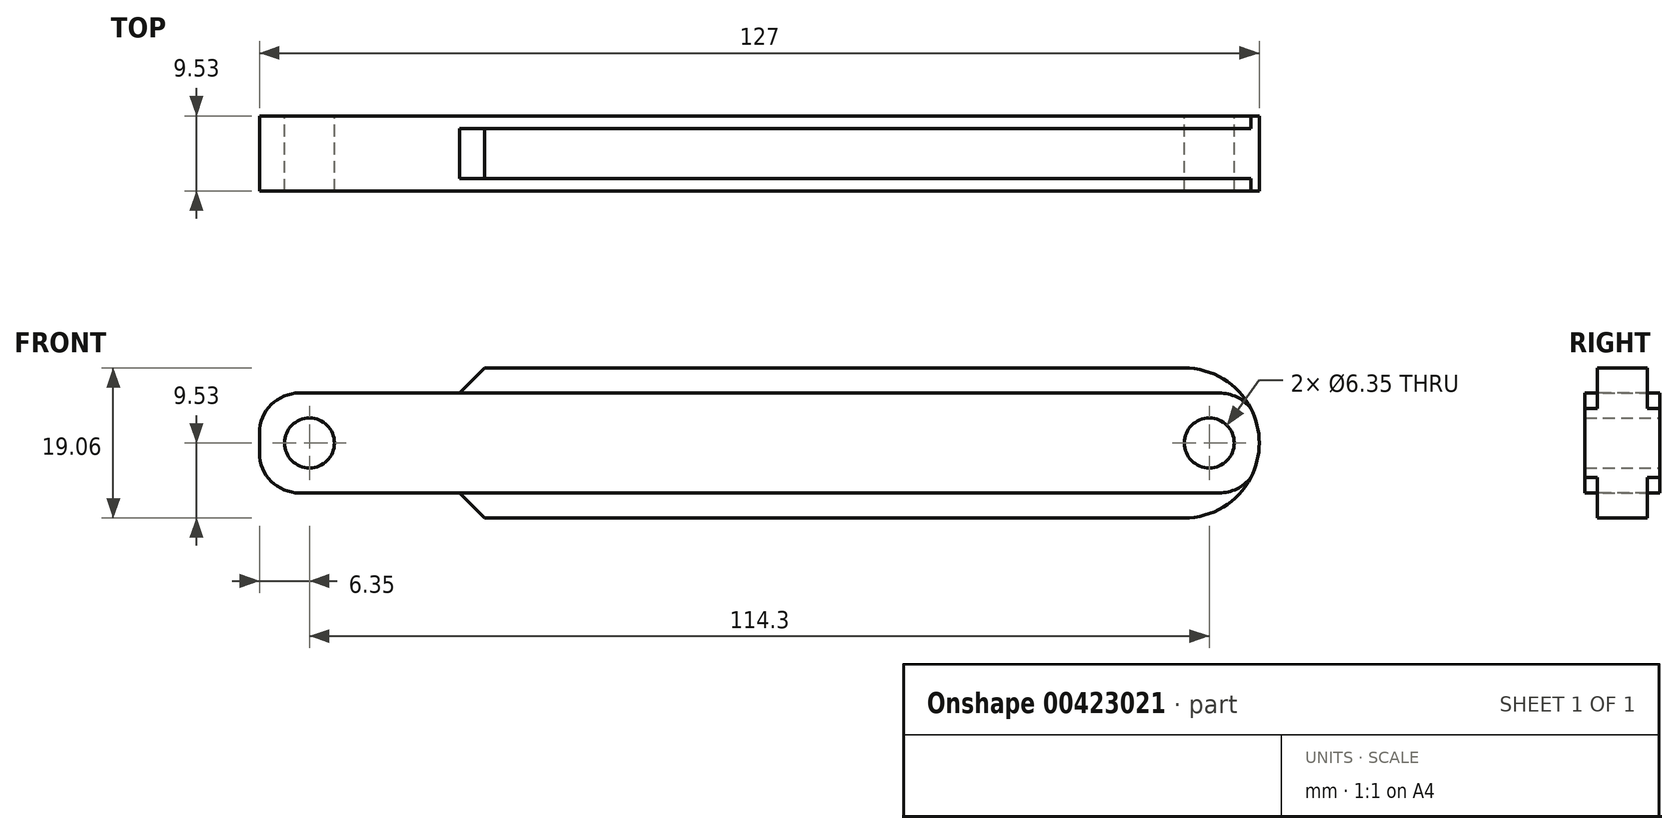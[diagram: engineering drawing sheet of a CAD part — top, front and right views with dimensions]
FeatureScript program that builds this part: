
annotation { "Feature Type Name" : "Feature", "Feature Type Description" : "" }
export const myFeature = defineFeature(function(context is Context, id is Id, definition is map)
    precondition{}
    {
        {
            var Q0;
            Q0=qCreatedBy(makeId("Front.planeOp"),FACE);
            var sketch = newSketch(context, id + "F0", { "sketchPlane" : qUnion([Q0])});
            skLineSegment(sketch, "E0.bottom", {"start": v(63.5, 6.35) * mm, "end": v(-63.5, 6.35) * mm});
            skLineSegment(sketch, "E0.top", {"start": v(63.5, -6.35) * mm, "end": v(-63.5, -6.35) * mm});
            skLineSegment(sketch, "E0.left", {"start": v(63.5, 6.35) * mm, "end": v(63.5, -6.35) * mm});
            skLineSegment(sketch, "E0.right", {"start": v(-63.5, 6.35) * mm, "end": v(-63.5, -6.35) * mm});
            skPoint(sketch, "E0.middle", {"position": v(0, 0) * mm});
            skCircle(sketch, "E1", {"center": v(-57.15, 0) * mm, "radius": 3.18 * mm});
            skCircle(sketch, "E2", {"center": v(57.15, 0) * mm, "radius": 3.18 * mm});
            skSolve(sketch);
        }
        {
            var Q0;
            Q0=qSketchRegion(id+"F0",true);
            extrude(context, id + "F1", {"entities" : qUnion([Q0]), "depth" : 9.52 * mm});
        }
        {
            var Q0;
            Q0=makeQuery(id+"F1.opExtrude","SWEPT_EDGE",EDGE,{"disambiguationData":[OSD([sQuery(id+"F0.wireOp",EDGE,"E0.bottom"),sQuery(id+"F0.wireOp",EDGE,"E0.right")])]});
            var Q1;
            Q1=makeQuery(id+"F1.opExtrude","SWEPT_EDGE",EDGE,{"disambiguationData":[OSD([sQuery(id+"F0.wireOp",EDGE,"E0.top"),sQuery(id+"F0.wireOp",EDGE,"E0.right")])]});
            var Q2;
            Q2=makeQuery(id+"F1.opExtrude","SWEPT_EDGE",EDGE,{"disambiguationData":[OSD([sQuery(id+"F0.wireOp",EDGE,"E0.bottom"),sQuery(id+"F0.wireOp",EDGE,"E0.left")])]});
            var Q3;
            Q3=makeQuery(id+"F1.opExtrude","SWEPT_EDGE",EDGE,{"disambiguationData":[OSD([sQuery(id+"F0.wireOp",EDGE,"E0.top"),sQuery(id+"F0.wireOp",EDGE,"E0.left")])]});
            fillet(context, id + "F2", {"entities" : qUnion([Q0, Q1, Q2, Q3]), "radius" : 5.08 * mm, "tangentPropagation" : true, "allowEdgeOverflow" : false});
        }
        {
            var Q0;
            Q0=qCreatedBy(makeId("Top.planeOp"),FACE);
            var sketch = newSketch(context, id + "F3", { "sketchPlane" : qUnion([Q0])});
            skLineSegment(sketch, "E3", {"start": v(-128.39, -4.76) * mm, "end": v(129.82, -4.76) * mm});
            skSolve(sketch);
        }
        {
            var Q0;
            Q0=qBodyType(qCreatedBy(id+"F3",EDGE),BodyType.WIRE);
            var Q1;
            Q1=makeQuery(id+"F1.opExtrude","SWEPT_FACE",FACE,{"disambiguationData":[OSD([sQuery(id+"F0.wireOp",EDGE,"E0.bottom")])]});
            cPlane(context, id + "F4", {"entities" : qUnion([Q0, Q1]), "cplaneType" : CPlaneType.LINE_ANGLE, "offset" : 25.4 * mm, "angle" : 90 * degree, "width" : 152.4 * mm, "height" : 152.4 * mm});
        }
        {
            var Q0;
            Q0=qCreatedBy(id+"F4.planeOp",FACE);
            var sketch = newSketch(context, id + "F5", { "sketchPlane" : qUnion([Q0])});
            skLineSegment(sketch, "E4.bottom", {"start": v(-63.5, -9.52) * mm, "end": v(38.1, -9.52) * mm});
            skLineSegment(sketch, "E4.top", {"start": v(-63.5, 9.53) * mm, "end": v(38.1, 9.53) * mm});
            skLineSegment(sketch, "E4.left", {"start": v(-63.5, -9.52) * mm, "end": v(-63.5, 9.53) * mm});
            skLineSegment(sketch, "E4.right", {"start": v(38.1, -9.52) * mm, "end": v(38.1, 9.53) * mm});
            skArc(sketch, "E5", {"start": v(-57.06, -4.04) * mm, "mid": v(-52.92, 0.1) * mm, "end": v(-57.1, 4.18) * mm});
            skArc(sketch, "E6", {"start": v(-57.1, 4.18) * mm, "mid": v(-61.27, 0.05) * mm, "end": v(-57.06, -4.04) * mm});
            skSolve(sketch);
        }
        {
            var Q0;
            Q0=makeQuery(id+"F5.imprint","IMPRINT",FACE,{"disambiguationData":[TD([[makeQuery(id+"F5.imprint","IMPRINT",EDGE,{"derivedFrom":sQuery(id+"F5.wireOp",EDGE,"E4.bottom")}),1.0]])]});
            extrude(context, id + "F6", {"entities" : qUnion([Q0]), "operationType" : NewBodyOperationType.ADD, "depth" : 3.17 * mm, "hasSecondDirection" : true, "secondDirectionOppositeDirection" : true, "secondDirectionDepth" : 3.17 * mm});
        }
        {
            var Q0;
            Q0=makeQuery(id+"F6.opExtrude","SWEPT_EDGE",EDGE,{"disambiguationData":[OSD([sQuery(id+"F5.wireOp",EDGE,"E4.top"),sQuery(id+"F5.wireOp",EDGE,"E4.right")])]});
            var Q1;
            Q1=makeQuery(id+"F6.opExtrude","SWEPT_EDGE",EDGE,{"disambiguationData":[OSD([sQuery(id+"F5.wireOp",EDGE,"E4.bottom"),sQuery(id+"F5.wireOp",EDGE,"E4.right")])]});
            chamfer(context, id + "F7", {"entities" : qUnion([Q0, Q1]), "width" : 3.17 * mm, "tangentPropagation" : true});
        }
        {
            var Q0;
            Q0=makeQuery(id+"F6.opExtrude","SWEPT_EDGE",EDGE,{"disambiguationData":[OSD([sQuery(id+"F5.wireOp",EDGE,"E4.top"),sQuery(id+"F5.wireOp",EDGE,"E4.left")])]});
            var Q1;
            Q1=makeQuery(id+"F6.opExtrude","SWEPT_EDGE",EDGE,{"disambiguationData":[OSD([sQuery(id+"F5.wireOp",EDGE,"E4.bottom"),sQuery(id+"F5.wireOp",EDGE,"E4.left")])]});
            fillet(context, id + "F8", {"entities" : qUnion([Q0, Q1]), "radius" : 9.52 * mm, "tangentPropagation" : true, "allowEdgeOverflow" : false});
        }
    });
